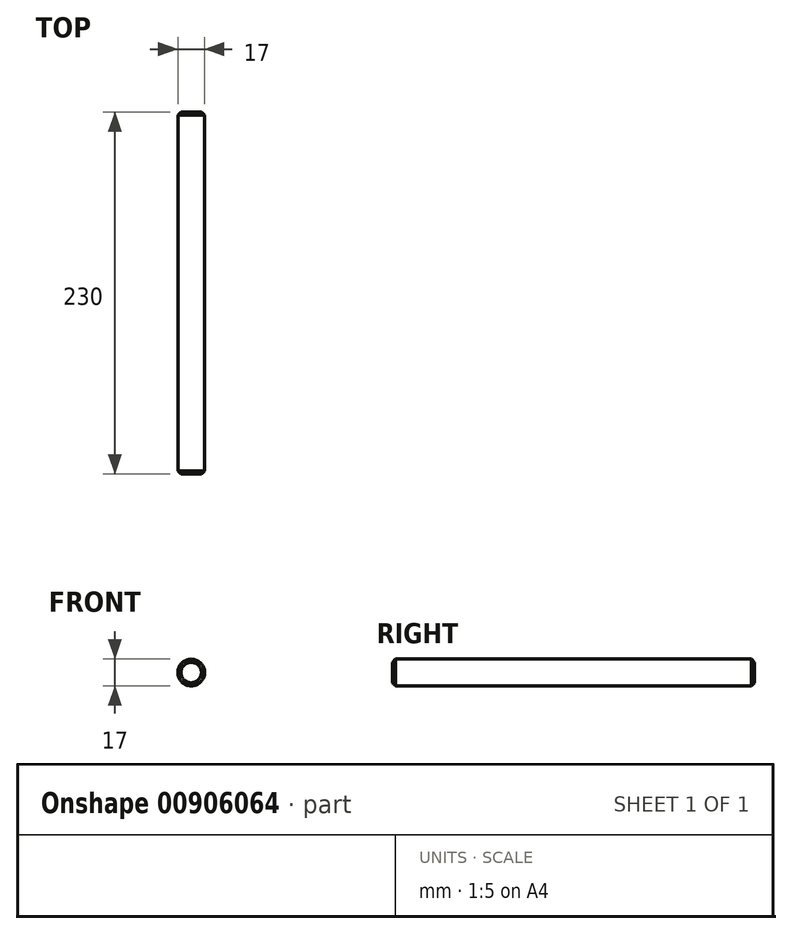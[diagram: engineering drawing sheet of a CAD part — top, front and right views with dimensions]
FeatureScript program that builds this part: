
annotation { "Feature Type Name" : "Feature", "Feature Type Description" : "" }
export const myFeature = defineFeature(function(context is Context, id is Id, definition is map)
    precondition{}
    {
        {
            var Q0;
            Q0=qCreatedBy(makeId("Front.planeOp"),FACE);
            var sketch = newSketch(context, id + "F0", { "sketchPlane" : qUnion([Q0])});
            skCircle(sketch, "E0", {"center": v(0, 0) * mm, "radius": 8.5 * mm});
            skSolve(sketch);
        }
        {
            var Q0;
            Q0 = qSketchRegion(id + "F0", true);
            extrude(context, id + "F1", {"entities" : qUnion([Q0]), "depth" : (100 + 65 + 65) * mm, "offsetDistance" : 25 * mm});
        }
        {
            var Q0;
            Q0=makeQuery(id+"F1.opExtrude","CAP_EDGE",EDGE,{"disambiguationData":[OSD([sQuery(id+"F0.wireOp",EDGE,"E0")])],"isStart":false});
            var Q1;
            Q1=makeQuery(id+"F1.opExtrude","CAP_EDGE",EDGE,{"disambiguationData":[OSD([sQuery(id+"F0.wireOp",EDGE,"E0")])],"isStart":true});
            chamfer(context, id + "F2", {"entities" : qUnion([Q0, Q1]), "width" : 2 * mm, "tangentPropagation" : true});
        }
    });
